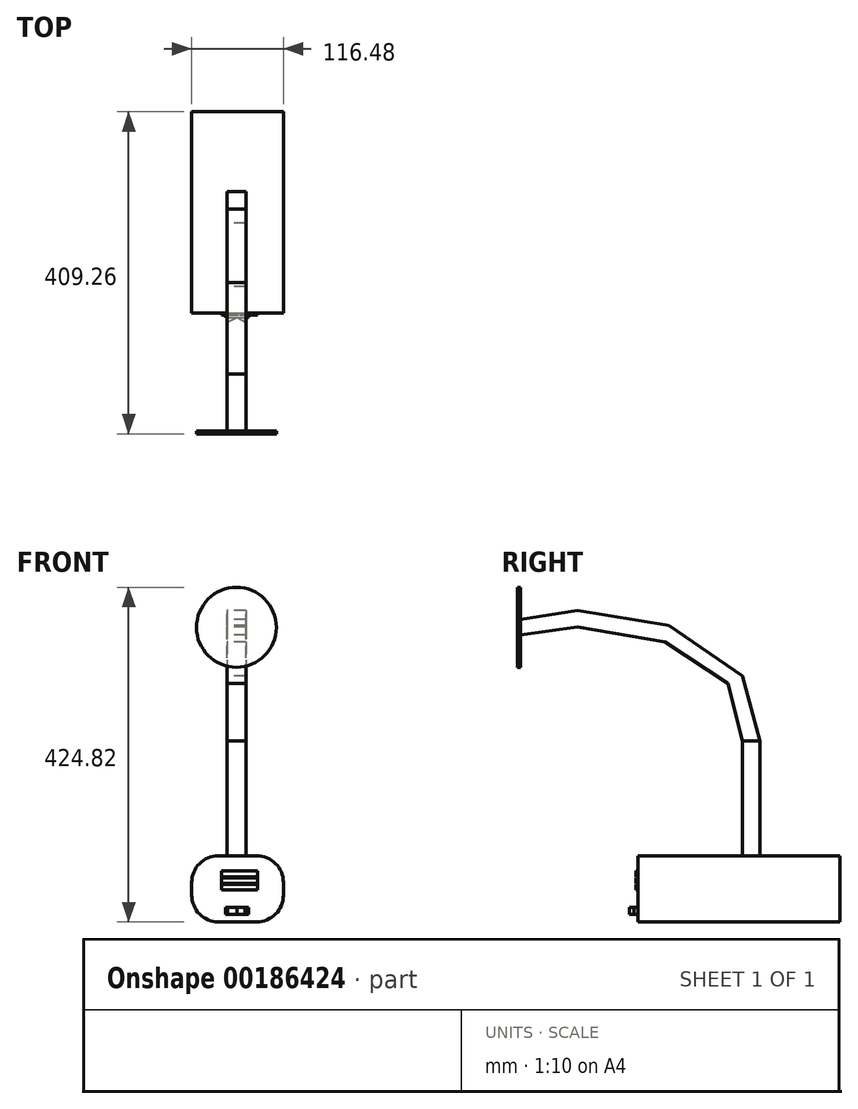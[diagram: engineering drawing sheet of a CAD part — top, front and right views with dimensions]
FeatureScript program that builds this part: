
annotation { "Feature Type Name" : "Feature", "Feature Type Description" : "" }
export const myFeature = defineFeature(function(context is Context, id is Id, definition is map)
    precondition{}
    {
        {
            var Q0;
            Q0=qCreatedBy(makeId("Front.planeOp"),FACE);
            var sketch = newSketch(context, id + "F0", { "sketchPlane" : qUnion([Q0])});
            skLineSegment(sketch, "E0.bottom", {"start": v(-35.02, -64.96) * mm, "end": v(81.46, -64.96) * mm});
            skLineSegment(sketch, "E0.top", {"start": v(-35.02, 18.73) * mm, "end": v(81.46, 18.73) * mm});
            skLineSegment(sketch, "E0.left", {"start": v(-35.02, -64.96) * mm, "end": v(-35.02, 18.73) * mm});
            skLineSegment(sketch, "E0.right", {"start": v(81.46, -64.96) * mm, "end": v(81.46, 18.73) * mm});
            skSolve(sketch);
        }
        {
            var Q0;
            Q0 = qSketchRegion(id + "F0", true);
            extrude(context, id + "F1", {"entities" : qUnion([Q0]), "oppositeDirection" : true, "depth" : 256.03 * mm});
        }
        {
            var Q0;
            Q0=makeQuery(id+"F1.opExtrude","SWEPT_FACE",FACE,{"disambiguationData":[OSD([sQuery(id+"F0.wireOp",EDGE,"E0.top")])]});
            var sketch = newSketch(context, id + "F2", { "sketchPlane" : qUnion([Q0])});
            skLineSegment(sketch, "E1.bottom", {"start": v(9.62, 132.44) * mm, "end": v(34.27, 132.44) * mm});
            skLineSegment(sketch, "E1.top", {"start": v(9.62, 154.63) * mm, "end": v(34.27, 154.63) * mm});
            skLineSegment(sketch, "E1.left", {"start": v(9.62, 132.44) * mm, "end": v(9.62, 154.63) * mm});
            skLineSegment(sketch, "E1.right", {"start": v(34.27, 132.44) * mm, "end": v(34.27, 154.63) * mm});
            skSolve(sketch);
        }
        {
            var Q0;
            Q0 = qSketchRegion(id + "F2", true);
            extrude(context, id + "F3", {"entities" : qUnion([Q0]), "operationType" : NewBodyOperationType.ADD, "depth" : 146.05 * mm});
        }
        {
            var Q0;
            Q0=makeQuery(id+"F3.opExtrude","SWEPT_FACE",FACE,{"disambiguationData":[OSD([sQuery(id+"F2.wireOp",EDGE,"E1.left")])]});
            var sketch = newSketch(context, id + "F4", { "sketchPlane" : qUnion([Q0])});
            skLineSegment(sketch, "E2", {"start": v(-154.63, 164.78) * mm, "end": v(-132.44, 247.53) * mm});
            skLineSegment(sketch, "E3", {"start": v(-132.44, 247.53) * mm, "end": v(-39.15, 311.32) * mm});
            skLineSegment(sketch, "E4", {"start": v(-39.15, 311.32) * mm, "end": v(77.05, 330.9) * mm});
            skLineSegment(sketch, "E5", {"start": v(77.05, 330.9) * mm, "end": v(149.67, 318.9) * mm});
            skLineSegment(sketch, "E6", {"start": v(149.67, 318.9) * mm, "end": v(149.67, 299.32) * mm});
            skLineSegment(sketch, "E7", {"start": v(149.67, 299.32) * mm, "end": v(77.05, 309.42) * mm});
            skLineSegment(sketch, "E8", {"start": v(77.05, 309.42) * mm, "end": v(-34.1, 290.48) * mm});
            skLineSegment(sketch, "E9", {"start": v(-34.1, 290.48) * mm, "end": v(-114.3, 238.06) * mm});
            skLineSegment(sketch, "E10", {"start": v(-114.3, 238.06) * mm, "end": v(-132.44, 164.78) * mm});
            skLineSegment(sketch, "E11", {"start": v(-132.44, 164.78) * mm, "end": v(-154.63, 164.78) * mm});
            skSolve(sketch);
        }
        {
            var Q0;
            Q0 = qSketchRegion(id + "F4", true);
            extrude(context, id + "F5", {"entities" : qUnion([Q0]), "operationType" : NewBodyOperationType.ADD, "oppositeDirection" : true, "depth" : 24.38 * mm});
        }
        {
            var Q0;
            Q0=makeQuery(id+"F1.opExtrude","SWEPT_EDGE",EDGE,{"disambiguationData":[OSD([sQuery(id+"F0.wireOp",EDGE,"E0.top"),sQuery(id+"F0.wireOp",EDGE,"E0.left")])]});
            var Q1;
            Q1=makeQuery(id+"F1.opExtrude","SWEPT_EDGE",EDGE,{"disambiguationData":[OSD([sQuery(id+"F0.wireOp",EDGE,"E0.top"),sQuery(id+"F0.wireOp",EDGE,"E0.right")])]});
            var Q2;
            Q2=makeQuery(id+"F1.opExtrude","SWEPT_EDGE",EDGE,{"disambiguationData":[OSD([sQuery(id+"F0.wireOp",EDGE,"E0.bottom"),sQuery(id+"F0.wireOp",EDGE,"E0.left")])]});
            var Q3;
            Q3=makeQuery(id+"F1.opExtrude","SWEPT_EDGE",EDGE,{"disambiguationData":[OSD([sQuery(id+"F0.wireOp",EDGE,"E0.bottom"),sQuery(id+"F0.wireOp",EDGE,"E0.right")])]});
            fillet(context, id + "F6", {"entities" : qUnion([Q0, Q1, Q2, Q3]), "radius" : 33.73 * mm, "tangentPropagation" : true, "allowEdgeOverflow" : false});
        }
        {
            var Q0;
            Q0=makeQuery(id+"F5.opExtrude","SWEPT_FACE",FACE,{"disambiguationData":[OSD([sQuery(id+"F4.wireOp",EDGE,"E6")])]});
            var sketch = newSketch(context, id + "F7", { "sketchPlane" : qUnion([Q0])});
            skCircle(sketch, "E12", {"center": v(21.8, 309.1) * mm, "radius": 51.15 * mm});
            skPoint(sketch, "E12.centerSnap0", {"position": v(21.8, 318.9) * mm});
            skPoint(sketch, "E12.centerSnap1", {"position": v(9.62, 309.1) * mm});
            skSolve(sketch);
        }
        {
            var Q0;
            Q0 = qSketchRegion(id + "F7", true);
            var Q1;
            Q1=sQuery(id+"F7.wireOp",EDGE,"E12");
            extrude(context, id + "F8", {"entities" : qUnion([Q0]), "bodyType" : ToolBodyType.SURFACE, "surfaceEntities" : qUnion([Q1]), "depth" : 113.03 * mm});
        }
        {
            var Q0;
            Q0=makeQuery(id+"F5.opExtrude","SWEPT_FACE",FACE,{"disambiguationData":[OSD([sQuery(id+"F4.wireOp",EDGE,"E6")])]});
            var sketch = newSketch(context, id + "F9", { "sketchPlane" : qUnion([Q0])});
            skCircle(sketch, "E13", {"center": v(21.8, 309.1) * mm, "radius": 50.76 * mm});
            skPoint(sketch, "E13.centerSnap0", {"position": v(21.8, 318.9) * mm});
            skPoint(sketch, "E13.centerSnap1", {"position": v(34, 309.1) * mm});
            skSolve(sketch);
        }
        {
            var Q0;
            Q0 = qSketchRegion(id + "F9", true);
            extrude(context, id + "F10", {"entities" : qUnion([Q0]), "operationType" : NewBodyOperationType.ADD, "depth" : 3.56 * mm});
        }
        {
            var Q0;
            Q0=makeQuery(id+"F1.opExtrude","CAP_FACE",FACE,{"disambiguationData":[OSD([sQuery(id+"F0.wireOp",EDGE,"E0.bottom"),sQuery(id+"F0.wireOp",EDGE,"E0.top"),sQuery(id+"F0.wireOp",EDGE,"E0.left"),sQuery(id+"F0.wireOp",EDGE,"E0.right")])],"isStart":true});
            var sketch = newSketch(context, id + "F11", { "sketchPlane" : qUnion([Q0])});
            skLineSegment(sketch, "E14.bottom", {"start": v(8.03, -55.26) * mm, "end": v(37.18, -55.26) * mm});
            skLineSegment(sketch, "E14.top", {"start": v(8.03, -46.63) * mm, "end": v(37.18, -46.63) * mm});
            skLineSegment(sketch, "E14.left", {"start": v(8.03, -55.26) * mm, "end": v(8.03, -46.63) * mm});
            skLineSegment(sketch, "E14.right", {"start": v(37.18, -55.26) * mm, "end": v(37.18, -46.63) * mm});
            skSolve(sketch);
        }
        {
            var Q0;
            Q0 = qSketchRegion(id + "F11", true);
            extrude(context, id + "F12", {"entities" : qUnion([Q0]), "operationType" : NewBodyOperationType.ADD, "depth" : 5.6 * mm});
        }
        {
            var Q0;
            Q0=makeQuery(id+"F12.opExtrude","SWEPT_FACE",FACE,{"disambiguationData":[OSD([sQuery(id+"F11.wireOp",EDGE,"E14.bottom")])]});
            var sketch = newSketch(context, id + "F13", { "sketchPlane" : qUnion([Q0])});
            skLineSegment(sketch, "E15", {"start": v(10.67, 5.59) * mm, "end": v(10.67, 11.09) * mm});
            skLineSegment(sketch, "E16", {"start": v(10.67, 11.09) * mm, "end": v(22.6, 5.59) * mm});
            skLineSegment(sketch, "E17", {"start": v(22.6, 5.59) * mm, "end": v(32.63, 11.09) * mm});
            skLineSegment(sketch, "E18", {"start": v(32.63, 11.09) * mm, "end": v(32.63, 5.59) * mm});
            skLineSegment(sketch, "E19", {"start": v(32.63, 5.59) * mm, "end": v(10.67, 5.59) * mm});
            skSolve(sketch);
        }
        {
            var Q0;
            Q0 = qSketchRegion(id + "F13", true);
            extrude(context, id + "F14", {"entities" : qUnion([Q0]), "operationType" : NewBodyOperationType.ADD, "oppositeDirection" : true, "depth" : 8.53 * mm});
        }
        {
            var Q0;
            Q0=makeQuery(id+"F1.opExtrude","CAP_FACE",FACE,{"disambiguationData":[OSD([sQuery(id+"F0.wireOp",EDGE,"E0.bottom"),sQuery(id+"F0.wireOp",EDGE,"E0.top"),sQuery(id+"F0.wireOp",EDGE,"E0.left"),sQuery(id+"F0.wireOp",EDGE,"E0.right")])],"isStart":true});
            var sketch = newSketch(context, id + "F15", { "sketchPlane" : qUnion([Q0])});
            skLineSegment(sketch, "E20.bottom", {"start": v(2.67, -24.54) * mm, "end": v(48.7, -24.54) * mm});
            skLineSegment(sketch, "E20.top", {"start": v(2.67, 0) * mm, "end": v(48.7, 0) * mm});
            skLineSegment(sketch, "E20.left", {"start": v(2.67, -24.54) * mm, "end": v(2.67, 0) * mm});
            skLineSegment(sketch, "E20.right", {"start": v(48.7, -24.54) * mm, "end": v(48.7, 0) * mm});
            skSolve(sketch);
        }
        {
            var Q0;
            Q0 = qSketchRegion(id + "F15", true);
            extrude(context, id + "F16", {"entities" : qUnion([Q0]), "operationType" : NewBodyOperationType.ADD, "depth" : 0.76 * mm});
        }
        {
            var Q0;
            Q0=makeQuery(id+"F16.opExtrude","CAP_FACE",FACE,{"disambiguationData":[OSD([sQuery(id+"F15.wireOp",EDGE,"E20.bottom"),sQuery(id+"F15.wireOp",EDGE,"E20.top"),sQuery(id+"F15.wireOp",EDGE,"E20.left"),sQuery(id+"F15.wireOp",EDGE,"E20.right")])],"isStart":false});
            var sketch = newSketch(context, id + "F17", { "sketchPlane" : qUnion([Q0])});
            skLineSegment(sketch, "E21.bottom", {"start": v(2.67, 0) * mm, "end": v(48.7, 0) * mm});
            skLineSegment(sketch, "E21.top", {"start": v(2.67, -8.09) * mm, "end": v(48.7, -8.09) * mm});
            skLineSegment(sketch, "E21.left", {"start": v(2.67, 0) * mm, "end": v(2.67, -8.09) * mm});
            skLineSegment(sketch, "E21.right", {"start": v(48.7, 0) * mm, "end": v(48.7, -8.09) * mm});
            skSolve(sketch);
        }
        {
            var Q0;
            Q0 = qSketchRegion(id + "F17", true);
            extrude(context, id + "F18", {"entities" : qUnion([Q0]), "operationType" : NewBodyOperationType.ADD, "depth" : 1.78 * mm});
        }
        {
            var Q0;
            Q0=makeQuery(id+"F16.opExtrude","CAP_FACE",FACE,{"disambiguationData":[OSD([sQuery(id+"F15.wireOp",EDGE,"E20.bottom"),sQuery(id+"F15.wireOp",EDGE,"E20.top"),sQuery(id+"F15.wireOp",EDGE,"E20.left"),sQuery(id+"F15.wireOp",EDGE,"E20.right")])],"isStart":false});
            var sketch = newSketch(context, id + "F19", { "sketchPlane" : qUnion([Q0])});
            skLineSegment(sketch, "E22.bottom", {"start": v(2.67, -9.1) * mm, "end": v(48.7, -9.1) * mm});
            skLineSegment(sketch, "E22.top", {"start": v(2.67, -16.31) * mm, "end": v(48.7, -16.31) * mm});
            skLineSegment(sketch, "E22.left", {"start": v(2.67, -9.1) * mm, "end": v(2.67, -16.31) * mm});
            skLineSegment(sketch, "E22.right", {"start": v(48.7, -9.1) * mm, "end": v(48.7, -16.31) * mm});
            skSolve(sketch);
        }
        {
            var Q0;
            Q0 = qSketchRegion(id + "F19", true);
            extrude(context, id + "F20", {"entities" : qUnion([Q0]), "operationType" : NewBodyOperationType.ADD, "depth" : 1.78 * mm});
        }
        {
            var Q0;
            {var subQ0=sQuery(id+"F15.wireOp",EDGE,"E20.right");var subQ1=sQuery(id+"F15.wireOp",EDGE,"E20.left");var subQ2=sQuery(id+"F15.wireOp",EDGE,"E20.bottom");Q0=makeQuery(id+"F20.boolean.opBoolean","SPLIT",FACE,{"disambiguationData":[TD([makeQuery(id+"F16.opExtrude","SWEPT_FACE",FACE,{"disambiguationData":[OSD([subQ2])]})])],"derivedFrom":makeQuery(id+"F16.opExtrude","CAP_FACE",FACE,{"disambiguationData":[OSD([subQ2,sQuery(id+"F15.wireOp",EDGE,"E20.top"),subQ1,subQ0])],"isStart":false})});}
            var sketch = newSketch(context, id + "F21", { "sketchPlane" : qUnion([Q0])});
            skLineSegment(sketch, "E23.bottom", {"start": v(2.67, -17.15) * mm, "end": v(48.7, -17.15) * mm});
            skLineSegment(sketch, "E23.top", {"start": v(2.67, -24.54) * mm, "end": v(48.7, -24.54) * mm});
            skLineSegment(sketch, "E23.left", {"start": v(2.67, -17.15) * mm, "end": v(2.67, -24.54) * mm});
            skLineSegment(sketch, "E23.right", {"start": v(48.7, -17.15) * mm, "end": v(48.7, -24.54) * mm});
            skSolve(sketch);
        }
        {
            var Q0;
            Q0 = qSketchRegion(id + "F21", true);
            extrude(context, id + "F22", {"entities" : qUnion([Q0]), "operationType" : NewBodyOperationType.ADD, "depth" : 1.78 * mm});
        }
    });
